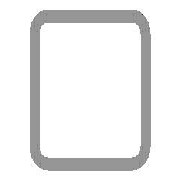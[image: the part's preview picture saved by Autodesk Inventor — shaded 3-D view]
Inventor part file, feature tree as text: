
AUTODESK INVENTOR PART (.ipt)
format: ipt  version: 2025 (Build 290162010, 162A)  size: 133,120 bytes
history: native  units: mm (DEFAULTED — no unit token found)
features: other x4, sketch x1, plane x1
ambient origin geometry x8: Origin, YZ Plane, XZ Plane, XY Plane, X Axis, Y Axis, Z Axis, Center Point
bodies: Solid1 (feature_tree), Body (feature_tree)
feature tree (6):
  parser-record x1  (decoder bookkeeping rows leaked as tree rows — omitted from the tree; the rows remain in map.json)
  other  "Driven Length"
  other  "Start Plane"
  other  "End Plane"
  sketch  "Sketch3"  dims[d3=898.0mm d4=0.0mm d7=4.0mm d9=40.0mm d11=40.0mm d12=2.0mm d13=40.0mm d14=938.0mm d15=20.0mm d16=20.0mm d17=90.0deg d18=898.0mm]
  plane  "Work Plane3"
